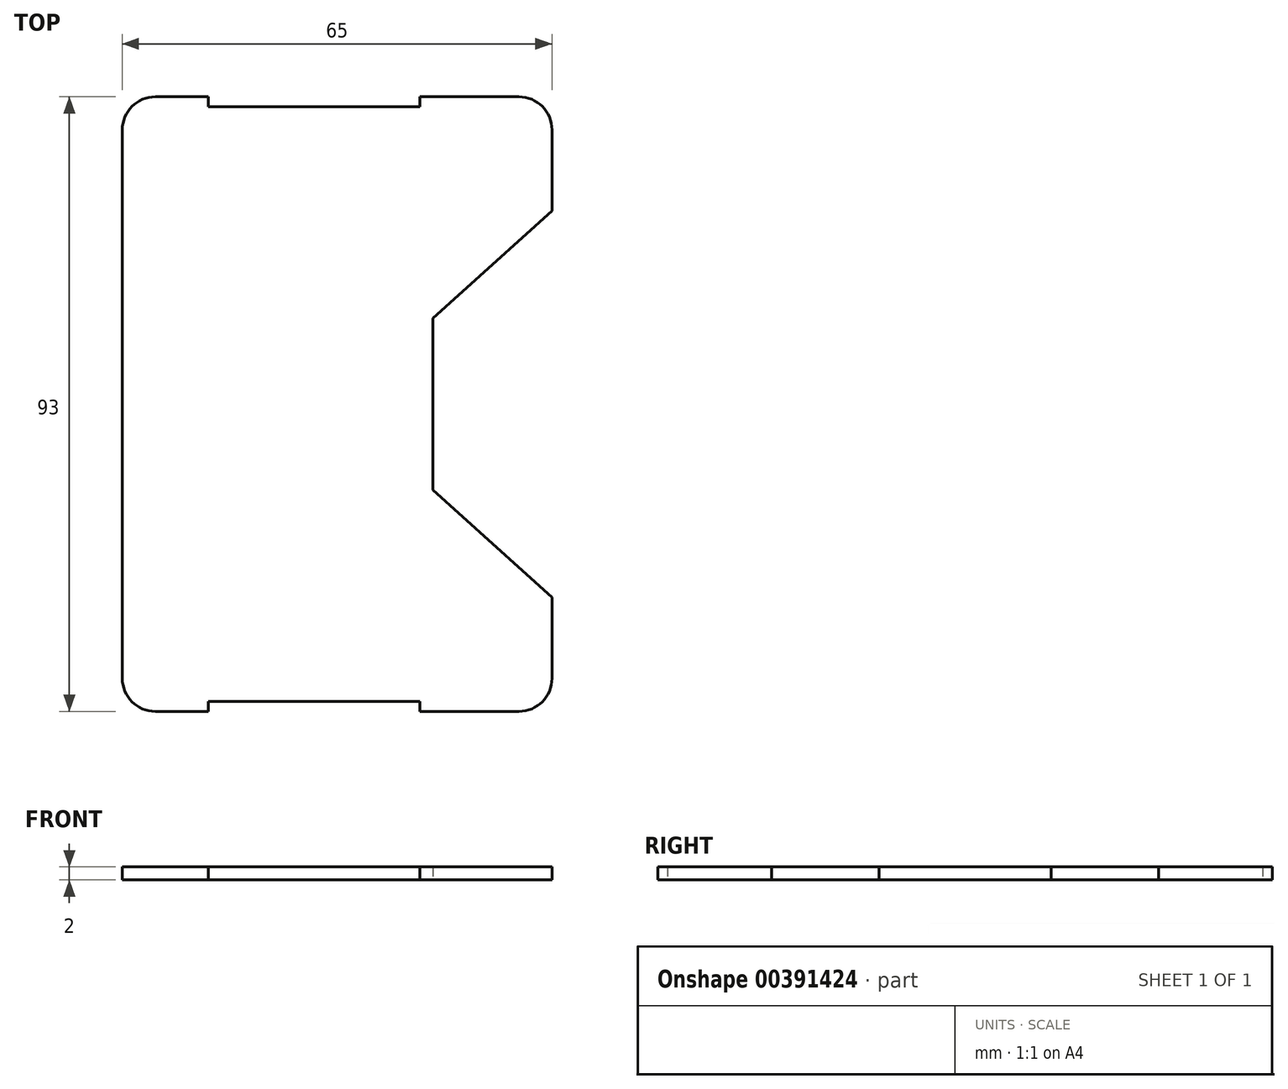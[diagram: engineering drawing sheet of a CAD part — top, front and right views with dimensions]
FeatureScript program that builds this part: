
annotation { "Feature Type Name" : "Feature", "Feature Type Description" : "" }
export const myFeature = defineFeature(function(context is Context, id is Id, definition is map)
    precondition{}
    {
        {
            var Q0;
            Q0=qCreatedBy(makeId("Top.planeOp"),FACE);
            var sketch = newSketch(context, id + "F0", { "sketchPlane" : qUnion([Q0])});
            skLineSegment(sketch, "E0.bottom", {"start": v(-36.98, 60.47) * mm, "end": v(28.02, 60.47) * mm});
            skLineSegment(sketch, "E0.top", {"start": v(-36.98, -32.53) * mm, "end": v(28.02, -32.53) * mm});
            skLineSegment(sketch, "E0.left", {"start": v(-36.98, 60.47) * mm, "end": v(-36.98, -32.53) * mm});
            skLineSegment(sketch, "E0.right", {"start": v(28.02, 60.47) * mm, "end": v(28.02, -32.53) * mm});
            skLineSegment(sketch, "E1", {"start": v(-36.98, 13.97) * mm, "end": v(36.75, 13.97) * mm, "construction": true});
            skPoint(sketch, "E1.endSnap0", {"position": v(28.02, 13.97) * mm});
            skLineSegment(sketch, "E2", {"start": v(28.02, 43.23) * mm, "end": v(10.02, 26.97) * mm});
            skLineSegment(sketch, "E3", {"start": v(10.02, 26.97) * mm, "end": v(10.02, 13.97) * mm});
            skLineSegment(sketch, "E4.MirrorCS", {"start": v(28.02, -15.3) * mm, "end": v(10.02, 0.97) * mm});
            skLineSegment(sketch, "E5.MirrorCS", {"start": v(10.02, 0.97) * mm, "end": v(10.02, 13.97) * mm});
            skLineSegment(sketch, "E6", {"start": v(10.02, 26.97) * mm, "end": v(10.02, 60.47) * mm, "construction": true});
            skLineSegment(sketch, "E7", {"start": v(8.02, 60.47) * mm, "end": v(8.02, 58.97) * mm});
            skLineSegment(sketch, "E8", {"start": v(8.02, 58.97) * mm, "end": v(-23.98, 58.97) * mm});
            skLineSegment(sketch, "E9", {"start": v(-23.98, 58.97) * mm, "end": v(-23.98, 60.47) * mm});
            skLineSegment(sketch, "E10.MirrorCS", {"start": v(-23.98, -31.03) * mm, "end": v(-23.98, -32.53) * mm});
            skLineSegment(sketch, "E11.MirrorCS", {"start": v(8.02, -31.03) * mm, "end": v(-23.98, -31.03) * mm});
            skLineSegment(sketch, "E12.MirrorCS", {"start": v(8.02, -32.53) * mm, "end": v(8.02, -31.03) * mm});
            skSolve(sketch);
        }
        {
            var Q0;
            {var subQ3=sQuery(id+"F0.wireOp",EDGE,"E0.left");Q0=makeQuery(id+"F0.imprint","IMPRINT",FACE,{"disambiguationData":[TD([[makeQuery(id+"F0.imprint","IMPRINT",EDGE,{"derivedFrom":subQ3}),1.0]])]});}
            extrude(context, id + "F1", {"entities" : qUnion([Q0]), "depth" : 2 * mm});
        }
        {
            var Q0;
            Q0=makeQuery(id+"F1.opExtrude","SWEPT_EDGE",EDGE,{"disambiguationData":[OSD([sQuery(id+"F0.wireOp",EDGE,"E0.top"),sQuery(id+"F0.wireOp",EDGE,"E0.left")])]});
            var Q1;
            Q1=makeQuery(id+"F1.opExtrude","SWEPT_EDGE",EDGE,{"disambiguationData":[OSD([sQuery(id+"F0.wireOp",EDGE,"E0.bottom"),sQuery(id+"F0.wireOp",EDGE,"E0.left")])]});
            var Q2;
            Q2=makeQuery(id+"F1.opExtrude","SWEPT_EDGE",EDGE,{"disambiguationData":[OSD([sQuery(id+"F0.wireOp",EDGE,"E0.bottom"),sQuery(id+"F0.wireOp",EDGE,"E0.right")])]});
            var Q3;
            Q3=makeQuery(id+"F1.opExtrude","SWEPT_EDGE",EDGE,{"disambiguationData":[OSD([sQuery(id+"F0.wireOp",EDGE,"E0.top"),sQuery(id+"F0.wireOp",EDGE,"E0.right")])]});
            fillet(context, id + "F2", {"entities" : qUnion([Q0, Q1, Q2, Q3]), "radius" : 5 * mm, "tangentPropagation" : true, "allowEdgeOverflow" : false});
        }
    });
